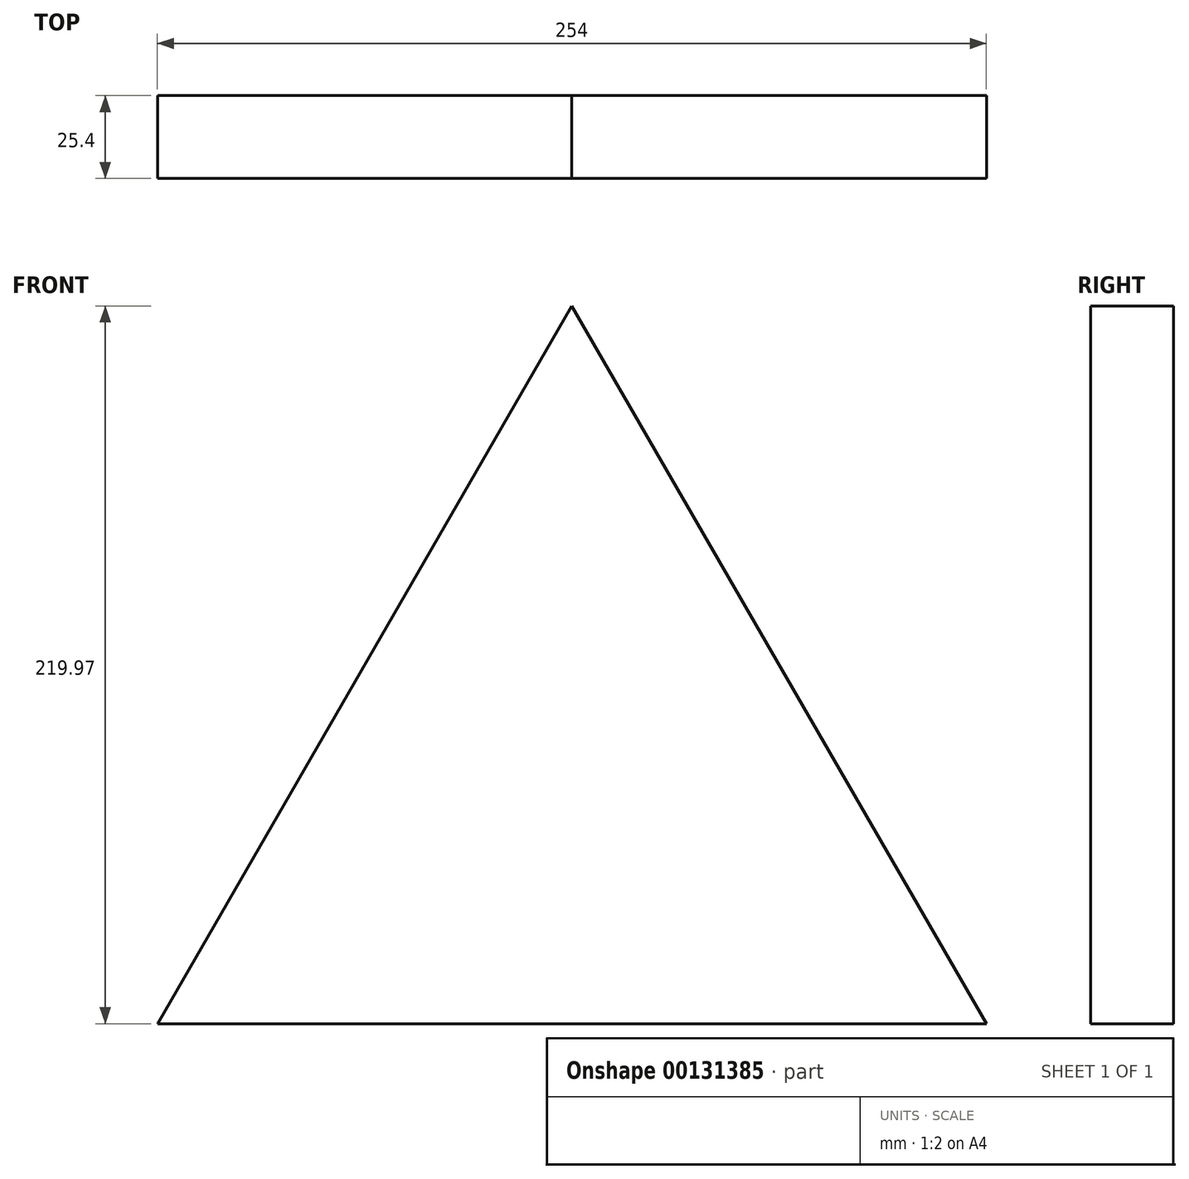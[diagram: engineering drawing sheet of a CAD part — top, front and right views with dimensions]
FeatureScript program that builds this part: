
annotation { "Feature Type Name" : "Feature", "Feature Type Description" : "" }
export const myFeature = defineFeature(function(context is Context, id is Id, definition is map)
    precondition{}
    {
        {
            var Q0;
            Q0=qCreatedBy(makeId("Front.planeOp"),FACE);
            var sketch = newSketch(context, id + "F0", { "sketchPlane" : qUnion([Q0])});
            skCircle(sketch, "E0.cCircle", {"center": v(0, -8.18) * mm, "radius": 73.32 * mm, "construction": true});
            skLineSegment(sketch, "E0.0", {"start": v(127, -81.5) * mm, "end": v(-127, -81.51) * mm});
            skLineSegment(sketch, "E0.1", {"start": v(-127, -81.51) * mm, "end": v(0, 138.46) * mm});
            skLineSegment(sketch, "E0.2", {"start": v(0, 138.46) * mm, "end": v(127, -81.5) * mm});
            skPoint(sketch, "E0.0.midPoint", {"position": v(0, -81.5) * mm});
            skLineSegment(sketch, "E1", {"start": v(-5.7, 128.6) * mm, "end": v(0, 138.46) * mm});
            skLineSegment(sketch, "E2", {"start": v(0, 138.46) * mm, "end": v(0, -81.5) * mm});
            skSolve(sketch);
        }
        {
            var Q0;
            Q0 = qSketchRegion(id + "F0", true);
            extrude(context, id + "F1", {"entities" : qUnion([Q0]), "depth" : 25.4 * mm});
        }
    });
